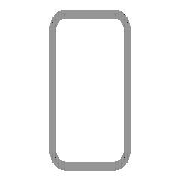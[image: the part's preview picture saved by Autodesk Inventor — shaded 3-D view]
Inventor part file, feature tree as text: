
AUTODESK INVENTOR PART (.ipt)
format: ipt  version: 2025.3 (Build 293356000, 356)  size: 133,632 bytes
history: native  units: mm (DEFAULTED — no unit token found)
features: other x4, sketch x1, plane x1
ambient origin geometry x8: Origin, YZ Plane, XZ Plane, XY Plane, X Axis, Y Axis, Z Axis, Center Point
bodies: Solid1 (feature_tree), Body (feature_tree)
feature tree (6):
  parser-record x1  (decoder bookkeeping rows leaked as tree rows — omitted from the tree; the rows remain in map.json)
  other  "Driven Length"
  other  "Start Plane"
  other  "End Plane"
  sketch  "Sketch3"  dims[d3=585.0mm d4=0.0mm d7=6.0mm d9=40.0mm d11=80.0mm d12=3.0mm d13=20.0mm d14=605.0mm d15=20.0mm d16=40.0mm d17=90.0deg d18=585.0mm]
  plane  "Work Plane3"
